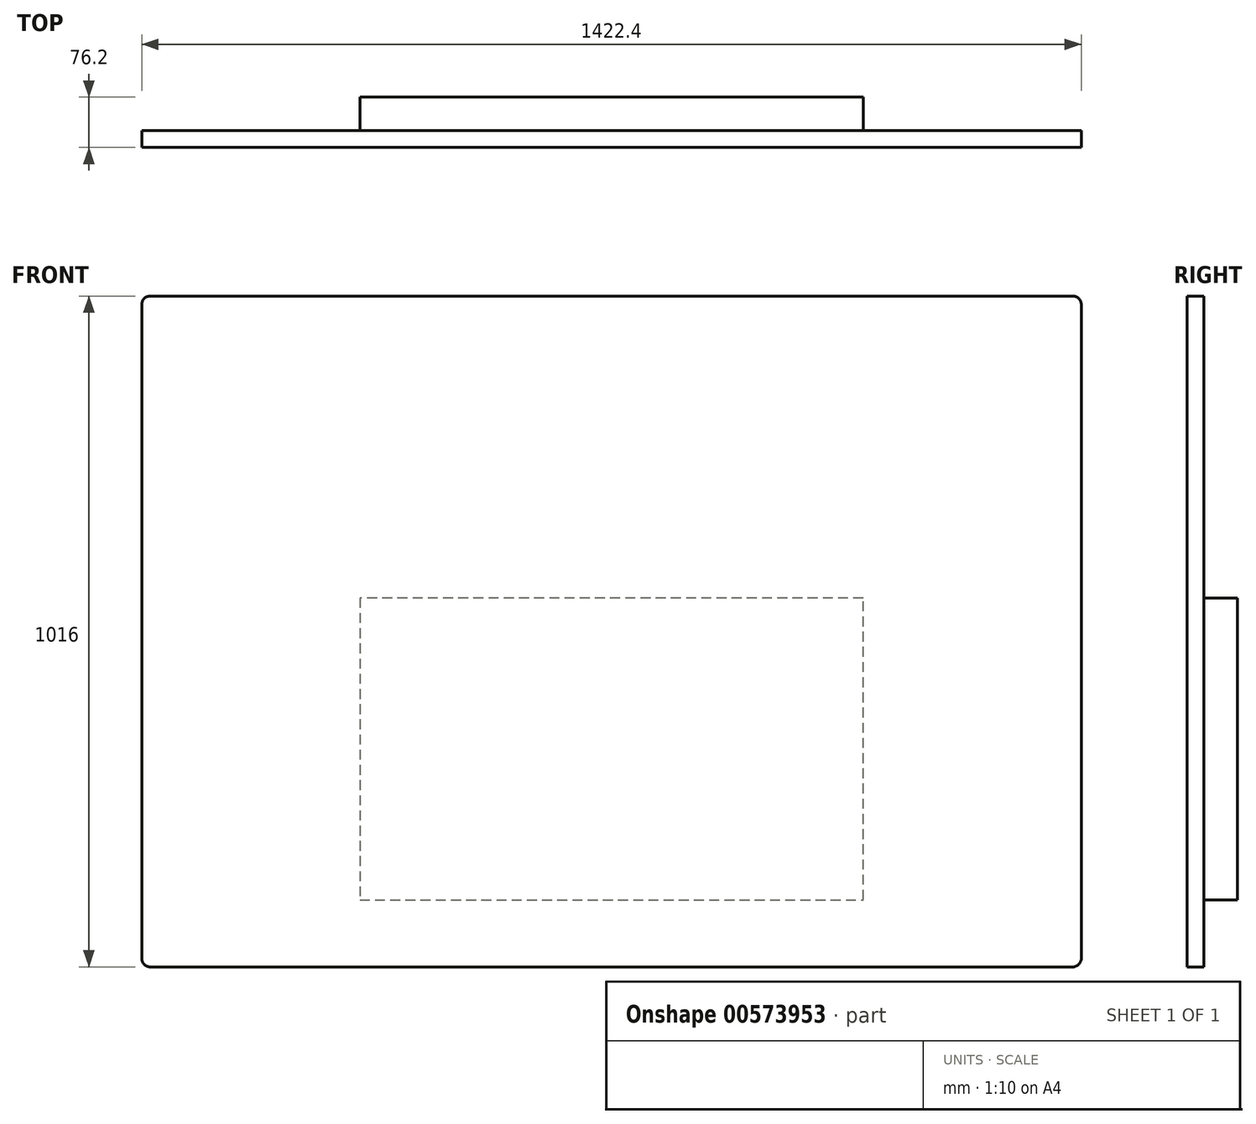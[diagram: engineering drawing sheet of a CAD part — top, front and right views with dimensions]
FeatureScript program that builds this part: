
annotation { "Feature Type Name" : "Feature", "Feature Type Description" : "" }
export const myFeature = defineFeature(function(context is Context, id is Id, definition is map)
    precondition{}
    {
        {
            var Q0;
            Q0=qCreatedBy(makeId("Front.planeOp"),FACE);
            var sketch = newSketch(context, id + "F0", { "sketchPlane" : qUnion([Q0])});
            skLineSegment(sketch, "E0.bottom", {"start": v(711.2, 508) * mm, "end": v(-711.2, 508) * mm});
            skLineSegment(sketch, "E0.top", {"start": v(711.2, -508) * mm, "end": v(-711.2, -508) * mm});
            skLineSegment(sketch, "E0.left", {"start": v(711.2, 508) * mm, "end": v(711.2, -508) * mm});
            skLineSegment(sketch, "E0.right", {"start": v(-711.2, 508) * mm, "end": v(-711.2, -508) * mm});
            skPoint(sketch, "E0.middle", {"position": v(0, 0) * mm});
            skLineSegment(sketch, "E1", {"start": v(-381, -406.4) * mm, "end": v(381, -406.4) * mm});
            skLineSegment(sketch, "E2", {"start": v(381, -406.4) * mm, "end": v(381, 50.8) * mm});
            skLineSegment(sketch, "E3", {"start": v(381, 50.8) * mm, "end": v(-381, 50.8) * mm});
            skLineSegment(sketch, "E4", {"start": v(-381, 50.8) * mm, "end": v(-381, -406.4) * mm});
            skSolve(sketch);
        }
        {
            var Q0;
            Q0=makeQuery(id+"F0.imprint","IMPRINT",FACE,{"disambiguationData":[TD([[makeQuery(id+"F0.imprint","IMPRINT",EDGE,{"derivedFrom":sQuery(id+"F0.wireOp",EDGE,"E1")}),1.0]])]});
            extrude(context, id + "F1", {"entities" : qUnion([Q0]), "oppositeDirection" : true, "depth" : 50.8 * mm, "offsetDistance" : 25.4 * mm});
        }
        {
            var Q0;
            Q0 = qSketchRegion(id + "F0", true);
            var Q1;
            Q1=makeQuery(id+"F1.opExtrude","CAP_FACE",FACE,{"disambiguationData":[OSD([sQuery(id+"F0.wireOp",EDGE,"E1"),sQuery(id+"F0.wireOp",EDGE,"E2"),sQuery(id+"F0.wireOp",EDGE,"E3"),sQuery(id+"F0.wireOp",EDGE,"E4")])],"isStart":true});
            extrude(context, id + "F2", {"entities" : qUnion([Q0, Q1]), "operationType" : NewBodyOperationType.ADD, "depth" : 25.4 * mm, "offsetDistance" : 25.4 * mm});
        }
        {
            var Q0;
            Q0=makeQuery(id+"F2.opExtrude","SWEPT_EDGE",EDGE,{"disambiguationData":[OSD([sQuery(id+"F0.wireOp",EDGE,"E0.top"),sQuery(id+"F0.wireOp",EDGE,"E0.left")])]});
            var Q1;
            Q1=makeQuery(id+"F2.opExtrude","SWEPT_EDGE",EDGE,{"disambiguationData":[OSD([sQuery(id+"F0.wireOp",EDGE,"E0.top"),sQuery(id+"F0.wireOp",EDGE,"E0.right")])]});
            var Q2;
            Q2=makeQuery(id+"F2.opExtrude","SWEPT_EDGE",EDGE,{"disambiguationData":[OSD([sQuery(id+"F0.wireOp",EDGE,"E0.bottom"),sQuery(id+"F0.wireOp",EDGE,"E0.right")])]});
            var Q3;
            Q3=makeQuery(id+"F2.opExtrude","SWEPT_EDGE",EDGE,{"disambiguationData":[OSD([sQuery(id+"F0.wireOp",EDGE,"E0.bottom"),sQuery(id+"F0.wireOp",EDGE,"E0.left")])]});
            fillet(context, id + "F3", {"entities" : qUnion([Q0, Q1, Q2, Q3]), "radius" : 12.7 * mm, "tangentPropagation" : true, "allowEdgeOverflow" : false});
        }
    });
